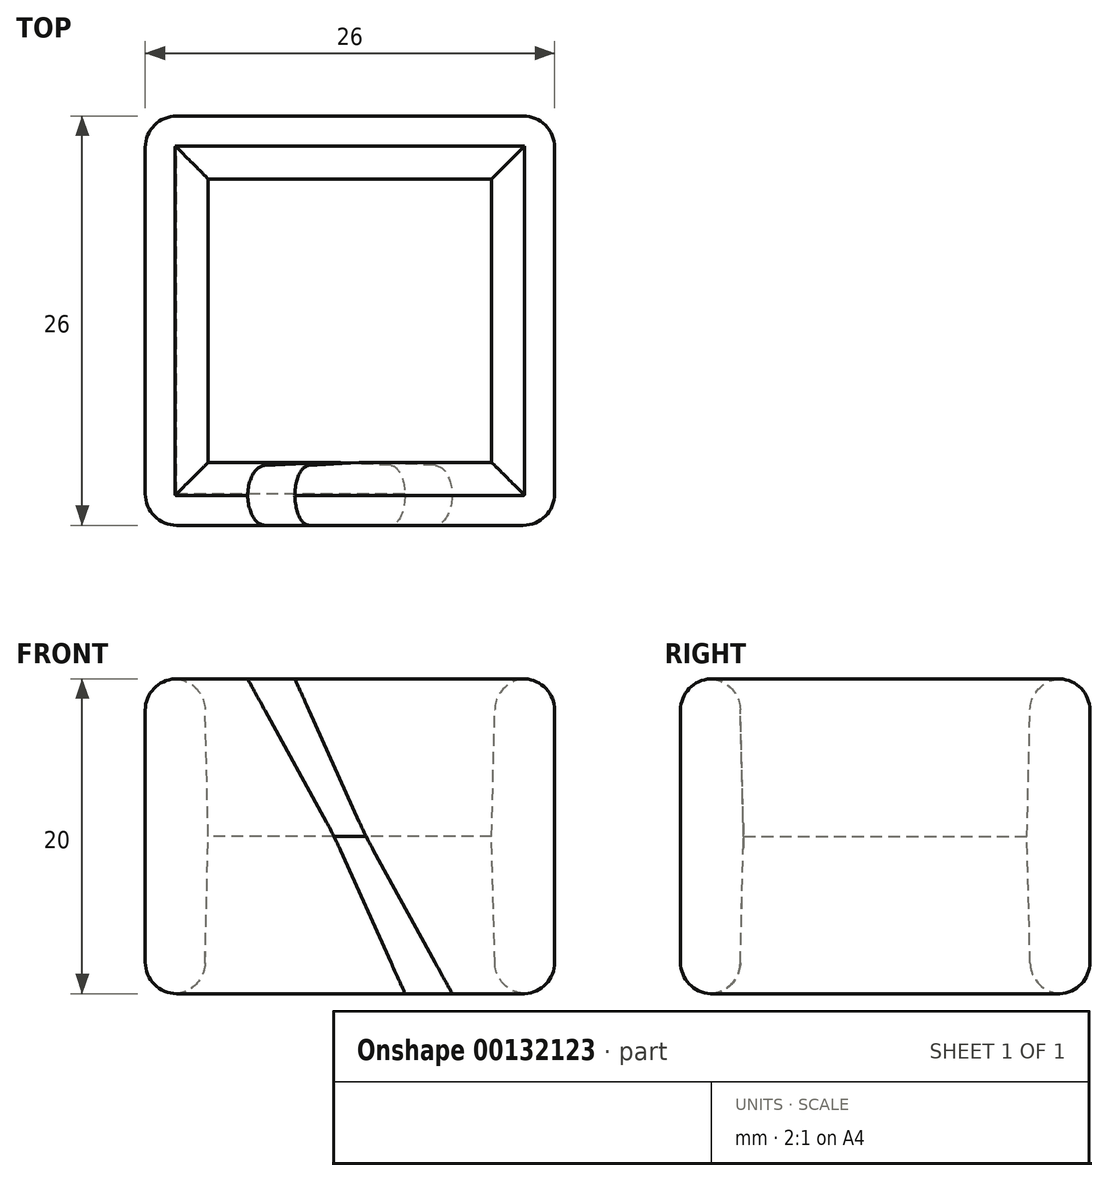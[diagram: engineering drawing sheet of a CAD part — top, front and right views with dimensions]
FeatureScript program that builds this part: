
annotation { "Feature Type Name" : "Feature", "Feature Type Description" : "" }
export const myFeature = defineFeature(function(context is Context, id is Id, definition is map)
    precondition{}
    {
        {
            var Q0;
            Q0=qCreatedBy(makeId("Top.planeOp"),FACE);
            var sketch = newSketch(context, id + "F0", { "sketchPlane" : qUnion([Q0])});
            skLineSegment(sketch, "E0.bottom", {"start": v(9.25, -9.25) * mm, "end": v(-9.25, -9.25) * mm});
            skLineSegment(sketch, "E0.top", {"start": v(9.25, 9.25) * mm, "end": v(-9.25, 9.25) * mm});
            skLineSegment(sketch, "E0.left", {"start": v(9.25, -9.25) * mm, "end": v(9.25, 9.25) * mm});
            skLineSegment(sketch, "E0.right", {"start": v(-9.25, -9.25) * mm, "end": v(-9.25, 9.25) * mm});
            skPoint(sketch, "E0.middle", {"position": v(0, 0) * mm});
            skLineSegment(sketch, "E1.bottom", {"start": v(13, -13) * mm, "end": v(-13, -13) * mm});
            skLineSegment(sketch, "E1.top", {"start": v(13, 13) * mm, "end": v(-13, 13) * mm});
            skLineSegment(sketch, "E1.left", {"start": v(13, -13) * mm, "end": v(13, 13) * mm});
            skLineSegment(sketch, "E1.right", {"start": v(-13, -13) * mm, "end": v(-13, 13) * mm});
            skLineSegment(sketch, "E2", {"start": v(-9.25, -9.25) * mm, "end": v(-13, -13) * mm});
            skLineSegment(sketch, "E3", {"start": v(9.25, 9.25) * mm, "end": v(13, 13) * mm});
            skLineSegment(sketch, "E4", {"start": v(0, -9.25) * mm, "end": v(0, -13) * mm, "construction": true});
            skLineSegment(sketch, "E5.0", {"start": v(5, -9.25) * mm, "end": v(5, -13.25) * mm, "construction": true});
            skLineSegment(sketch, "E6.0", {"start": v(6.5, -9.25) * mm, "end": v(6.5, -13.25) * mm});
            skLineSegment(sketch, "E7.0", {"start": v(3.5, -9.25) * mm, "end": v(3.5, -13.25) * mm});
            skSolve(sketch);
        }
        {
            var Q0;
            Q0=qCreatedBy(makeId("Top.planeOp"),FACE);
            cPlane(context, id + "F1", {"entities" : qUnion([Q0]), "cplaneType" : CPlaneType.OFFSET, "offset" : 10 * mm, "width" : 150 * mm, "height" : 150 * mm});
        }
        {
            var Q0;
            Q0=qCreatedBy(id+"F1.planeOp",FACE);
            var sketch = newSketch(context, id + "F2", { "sketchPlane" : qUnion([Q0])});
            skPoint(sketch, "E8.0", {"position": v(0, 0) * mm});
            skLineSegment(sketch, "E9.0", {"start": v(13, 13) * mm, "end": v(-13, 13) * mm});
            skLineSegment(sketch, "E10.0", {"start": v(-13, -13) * mm, "end": v(-13, 13) * mm});
            skLineSegment(sketch, "E11.0", {"start": v(13, -13) * mm, "end": v(-13, -13) * mm});
            skLineSegment(sketch, "E12.0", {"start": v(13, -13) * mm, "end": v(13, 13) * mm});
            skLineSegment(sketch, "E13.bottom", {"start": v(9, -9) * mm, "end": v(-9, -9) * mm});
            skLineSegment(sketch, "E13.top", {"start": v(9, 9) * mm, "end": v(-9, 9) * mm});
            skLineSegment(sketch, "E13.left", {"start": v(9, -9) * mm, "end": v(9, 9) * mm});
            skLineSegment(sketch, "E13.right", {"start": v(-9, -9) * mm, "end": v(-9, 9) * mm});
            skLineSegment(sketch, "E14", {"start": v(-13, -13) * mm, "end": v(-9, -9) * mm});
            skLineSegment(sketch, "E15", {"start": v(9, 9) * mm, "end": v(13, 13) * mm});
            skLineSegment(sketch, "E16", {"start": v(0, -9) * mm, "end": v(0, -13) * mm, "construction": true});
            skLineSegment(sketch, "E17.0", {"start": v(-1, -9) * mm, "end": v(-1, -13) * mm});
            skLineSegment(sketch, "E18.MirrorCS", {"start": v(1, -9) * mm, "end": v(1, -13) * mm});
            skSolve(sketch);
        }
        {
            var Q0;
            Q0=qCreatedBy(makeId("Top.planeOp"),FACE);
            cPlane(context, id + "F3", {"entities" : qUnion([Q0]), "cplaneType" : CPlaneType.OFFSET, "offset" : 20 * mm, "width" : 150 * mm, "height" : 150 * mm});
        }
        {
            var Q0;
            Q0=qCreatedBy(id+"F3.planeOp",FACE);
            var sketch = newSketch(context, id + "F4", { "sketchPlane" : qUnion([Q0])});
            skPoint(sketch, "E19.0", {"position": v(0, 0) * mm});
            skLineSegment(sketch, "E20.0", {"start": v(13, 13) * mm, "end": v(-13, 13) * mm});
            skLineSegment(sketch, "E21.0", {"start": v(13, -13) * mm, "end": v(13, 13) * mm});
            skLineSegment(sketch, "E21.1", {"start": v(13, -13) * mm, "end": v(-13, -13) * mm});
            skLineSegment(sketch, "E21.2", {"start": v(-13, -13) * mm, "end": v(-13, 13) * mm});
            skLineSegment(sketch, "E22.bottom", {"start": v(9.25, -9.25) * mm, "end": v(-9.25, -9.25) * mm});
            skLineSegment(sketch, "E22.top", {"start": v(9.25, 9.25) * mm, "end": v(-9.25, 9.25) * mm});
            skLineSegment(sketch, "E22.left", {"start": v(9.25, -9.25) * mm, "end": v(9.25, 9.25) * mm});
            skLineSegment(sketch, "E22.right", {"start": v(-9.25, -9.25) * mm, "end": v(-9.25, 9.25) * mm});
            skLineSegment(sketch, "E23", {"start": v(-13, -13) * mm, "end": v(-9.25, -9.25) * mm});
            skLineSegment(sketch, "E24", {"start": v(9.25, 9.25) * mm, "end": v(13, 13) * mm});
            skLineSegment(sketch, "E25", {"start": v(0, -9.25) * mm, "end": v(0, -13) * mm, "construction": true});
            skLineSegment(sketch, "E26.0", {"start": v(-5, -9.25) * mm, "end": v(-5, -13) * mm, "construction": true});
            skLineSegment(sketch, "E27.0", {"start": v(-6.5, -9.25) * mm, "end": v(-6.5, -13) * mm});
            skLineSegment(sketch, "E28.0", {"start": v(-3.5, -9.25) * mm, "end": v(-3.5, -13) * mm});
            skSolve(sketch);
        }
        {
            var Q0;
            Q0=makeQuery(id+"F0.imprint","IMPRINT",FACE,{"disambiguationData":[TD([[makeQuery(id+"F0.imprint","IMPRINT",EDGE,{"derivedFrom":sQuery(id+"F0.wireOp",EDGE,"E0.top")}),-1.0]])]});
            var Q1;
            Q1=makeQuery(id+"F2.imprint","IMPRINT",FACE,{"disambiguationData":[TD([[makeQuery(id+"F2.imprint","IMPRINT",EDGE,{"derivedFrom":sQuery(id+"F2.wireOp",EDGE,"E9.0")}),1.0]])]});
            loft(context, id + "F5", {"sheetProfilesArray" : [{ "sheetProfileEntities" : qUnion([Q0]) }, { "sheetProfileEntities" : qUnion([Q1]) }]});
        }
        {
            var Q1;
            Q1=makeQuery(id+"F2.imprint","IMPRINT",FACE,{"disambiguationData":[TD([[makeQuery(id+"F2.imprint","IMPRINT",EDGE,{"derivedFrom":sQuery(id+"F2.wireOp",EDGE,"E9.0")}),1.0]])]});
            var Q2;
            Q2=makeQuery(id+"F4.imprint","IMPRINT",FACE,{"disambiguationData":[TD([[makeQuery(id+"F4.imprint","IMPRINT",EDGE,{"derivedFrom":sQuery(id+"F4.wireOp",EDGE,"E20.0")}),1.0]])]});
            loft(context, id + "F6", {"operationType" : NewBodyOperationType.ADD, "sheetProfilesArray" : [{ "sheetProfileEntities" : qUnion([Q1]) }, { "sheetProfileEntities" : qUnion([Q2]) }]});
        }
        {
            var Q1;
            {var subQ0=sQuery(id+"F0.wireOp",EDGE,"E2");Q1=makeQuery(id+"F0.imprint","IMPRINT",FACE,{"disambiguationData":[TD([[makeQuery(id+"F0.imprint","IMPRINT",EDGE,{"derivedFrom":subQ0}),1.0]])]});}
            var Q2;
            {var subQ0=sQuery(id+"F2.wireOp",EDGE,"E14");Q2=makeQuery(id+"F2.imprint","IMPRINT",FACE,{"disambiguationData":[TD([[makeQuery(id+"F2.imprint","IMPRINT",EDGE,{"derivedFrom":subQ0}),-1.0]])]});}
            loft(context, id + "F7", {"operationType" : NewBodyOperationType.ADD, "sheetProfilesArray" : [{ "sheetProfileEntities" : qUnion([Q1]) }, { "sheetProfileEntities" : qUnion([Q2]) }]});
        }
        {
            var Q1;
            {var subQ0=sQuery(id+"F2.wireOp",EDGE,"E14");Q1=makeQuery(id+"F2.imprint","IMPRINT",FACE,{"disambiguationData":[TD([[makeQuery(id+"F2.imprint","IMPRINT",EDGE,{"derivedFrom":subQ0}),-1.0]])]});}
            var Q2;
            {var subQ0=sQuery(id+"F4.wireOp",EDGE,"E23");Q2=makeQuery(id+"F4.imprint","IMPRINT",FACE,{"disambiguationData":[TD([[makeQuery(id+"F4.imprint","IMPRINT",EDGE,{"derivedFrom":subQ0}),-1.0]])]});}
            loft(context, id + "F8", {"operationType" : NewBodyOperationType.ADD, "sheetProfilesArray" : [{ "sheetProfileEntities" : qUnion([Q1]) }, { "sheetProfileEntities" : qUnion([Q2]) }]});
        }
        {
            var Q1;
            {var subQ3=sQuery(id+"F0.wireOp",EDGE,"E0.left");Q1=makeQuery(id+"F0.imprint","IMPRINT",FACE,{"disambiguationData":[TD([[makeQuery(id+"F0.imprint","IMPRINT",EDGE,{"derivedFrom":subQ3}),-1.0]])]});}
            var Q2;
            {var subQ3=sQuery(id+"F2.wireOp",EDGE,"E12.0");Q2=makeQuery(id+"F2.imprint","IMPRINT",FACE,{"disambiguationData":[TD([[makeQuery(id+"F2.imprint","IMPRINT",EDGE,{"derivedFrom":subQ3}),1.0]])]});}
            loft(context, id + "F9", {"operationType" : NewBodyOperationType.ADD, "sheetProfilesArray" : [{ "sheetProfileEntities" : qUnion([Q1]) }, { "sheetProfileEntities" : qUnion([Q2]) }]});
        }
        {
            var Q1;
            {var subQ3=sQuery(id+"F2.wireOp",EDGE,"E12.0");Q1=makeQuery(id+"F2.imprint","IMPRINT",FACE,{"disambiguationData":[TD([[makeQuery(id+"F2.imprint","IMPRINT",EDGE,{"derivedFrom":subQ3}),1.0]])]});}
            var Q2;
            {var subQ4=sQuery(id+"F4.wireOp",EDGE,"E21.0");Q2=makeQuery(id+"F4.imprint","IMPRINT",FACE,{"disambiguationData":[TD([[makeQuery(id+"F4.imprint","IMPRINT",EDGE,{"derivedFrom":subQ4}),1.0]])]});}
            loft(context, id + "F10", {"operationType" : NewBodyOperationType.ADD, "sheetProfilesArray" : [{ "sheetProfileEntities" : qUnion([Q1]) }, { "sheetProfileEntities" : qUnion([Q2]) }]});
        }
        {
            var Q0;
            Q0=makeQuery(id+"F6.opLoft","MID_CAP_EDGE",EDGE,{"disambiguationData":[OSD([sQuery(id+"F4.wireOp",EDGE,"E22.top"),sQuery(id+"F4.wireOp",EDGE,"E22.left"),sQuery(id+"F4.wireOp",EDGE,"E22.right"),sQuery(id+"F4.wireOp",EDGE,"E24")])],"capPos":1.0});
            var Q1;
            Q1=makeQuery(id+"F10.opLoft","MID_CAP_EDGE",EDGE,{"disambiguationData":[OSD([sQuery(id+"F4.wireOp",EDGE,"E22.bottom"),sQuery(id+"F4.wireOp",EDGE,"E22.top"),sQuery(id+"F4.wireOp",EDGE,"E22.left"),sQuery(id+"F4.wireOp",EDGE,"E24")])],"capPos":1.0});
            var Q2;
            Q2=makeQuery(id+"F10.opLoft","MID_CAP_EDGE",EDGE,{"disambiguationData":[OSD([sQuery(id+"F4.wireOp",EDGE,"E22.bottom"),sQuery(id+"F4.wireOp",EDGE,"E22.left"),sQuery(id+"F4.wireOp",EDGE,"ebbac85e-4af3-46f9-9d82-f182fd674b780.MirrorCS")])],"capPos":1.0});
            var Q3;
            Q3=makeQuery(id+"F6.opLoft","MID_CAP_EDGE",EDGE,{"disambiguationData":[OSD([sQuery(id+"F4.wireOp",EDGE,"E22.bottom"),sQuery(id+"F4.wireOp",EDGE,"E22.top"),sQuery(id+"F4.wireOp",EDGE,"E22.right"),sQuery(id+"F4.wireOp",EDGE,"E23")])],"capPos":1.0});
            var Q4;
            Q4=makeQuery(id+"F8.opLoft","MID_CAP_EDGE",EDGE,{"disambiguationData":[OSD([sQuery(id+"F4.wireOp",EDGE,"E22.bottom"),sQuery(id+"F4.wireOp",EDGE,"E22.right"),sQuery(id+"F4.wireOp",EDGE,"E23"),sQuery(id+"F4.wireOp",EDGE,"E27.0")])],"capPos":1.0});
            var Q5;
            Q5=makeQuery(id+"F6.opLoft","MID_CAP_EDGE",EDGE,{"disambiguationData":[OSD([sQuery(id+"F4.wireOp",EDGE,"E20.0"),sQuery(id+"F4.wireOp",EDGE,"E21.1"),sQuery(id+"F4.wireOp",EDGE,"E21.2"),sQuery(id+"F4.wireOp",EDGE,"E23")])],"capPos":1.0});
            var Q6;
            Q6=makeQuery(id+"F8.opLoft","MID_CAP_EDGE",EDGE,{"disambiguationData":[OSD([sQuery(id+"F4.wireOp",EDGE,"E21.1"),sQuery(id+"F4.wireOp",EDGE,"E21.2"),sQuery(id+"F4.wireOp",EDGE,"E23"),sQuery(id+"F4.wireOp",EDGE,"E27.0")])],"capPos":1.0});
            var Q7;
            Q7=makeQuery(id+"F10.opLoft","MID_CAP_EDGE",EDGE,{"disambiguationData":[OSD([sQuery(id+"F4.wireOp",EDGE,"E21.0"),sQuery(id+"F4.wireOp",EDGE,"E21.1"),sQuery(id+"F4.wireOp",EDGE,"ebbac85e-4af3-46f9-9d82-f182fd674b780.MirrorCS")])],"capPos":1.0});
            var Q8;
            Q8=makeQuery(id+"F6.opLoft","MID_CAP_EDGE",EDGE,{"disambiguationData":[OSD([sQuery(id+"F4.wireOp",EDGE,"E20.0"),sQuery(id+"F4.wireOp",EDGE,"E21.0"),sQuery(id+"F4.wireOp",EDGE,"E21.2"),sQuery(id+"F4.wireOp",EDGE,"E24")])],"capPos":1.0});
            var Q9;
            Q9=makeQuery(id+"F10.opLoft","MID_CAP_EDGE",EDGE,{"disambiguationData":[OSD([sQuery(id+"F4.wireOp",EDGE,"E20.0"),sQuery(id+"F4.wireOp",EDGE,"E21.0"),sQuery(id+"F4.wireOp",EDGE,"E21.1"),sQuery(id+"F4.wireOp",EDGE,"E24")])],"capPos":1.0});
            var Q10;
            {var subQ0=sQuery(id+"F4.wireOp",EDGE,"E24");var subQ1=sQuery(id+"F4.wireOp",EDGE,"E21.0");var subQ2=sQuery(id+"F4.wireOp",EDGE,"E20.0");var subQ3=sQuery(id+"F2.wireOp",EDGE,"E15");var subQ4=sQuery(id+"F2.wireOp",EDGE,"E12.0");var subQ5=sQuery(id+"F2.wireOp",EDGE,"E9.0");var subQ6=sQuery(id+"F0.wireOp",EDGE,"E3");var subQ7=sQuery(id+"F0.wireOp",EDGE,"E1.left");var subQ8=sQuery(id+"F0.wireOp",EDGE,"E1.top");var subQ9=makeQuery(id+"F6.boolean.opBoolean","MERGE",EDGE,{"derivedFrom":[makeQuery(id+"F5.opLoft","SWEPT_EDGE",EDGE,{"disambiguationData":[OSD([subQ8,subQ7,subQ6,subQ5,subQ4,subQ3])]}),makeQuery(id+"F6.opLoft","SWEPT_EDGE",EDGE,{"disambiguationData":[OSD([subQ5,subQ4,subQ3,subQ2,subQ1,subQ0])]})]});Q10=makeQuery(id+"F10.boolean.opBoolean","MERGE",EDGE,{"derivedFrom":[makeQuery(id+"F9.boolean.opBoolean","MERGE",EDGE,{"derivedFrom":[subQ9,makeQuery(id+"F9.opLoft","SWEPT_EDGE",EDGE,{"disambiguationData":[OSD([subQ8,subQ7,subQ6,subQ5,subQ4,subQ3])]})]}),makeQuery(id+"F9.boolean.opBoolean","SPLIT",EDGE,{"derivedFrom":subQ9}),makeQuery(id+"F10.opLoft","SWEPT_EDGE",EDGE,{"disambiguationData":[OSD([subQ5,subQ4,subQ3,subQ2,subQ1,subQ0])]})]});}
            var Q11;
            {var subQ0=sQuery(id+"F2.wireOp",EDGE,"E12.0");var subQ1=sQuery(id+"F2.wireOp",EDGE,"E11.0");Q11=makeQuery(id+"F10.boolean.opBoolean","MERGE",EDGE,{"derivedFrom":[makeQuery(id+"F9.opLoft","SWEPT_EDGE",EDGE,{"disambiguationData":[OSD([sQuery(id+"F0.wireOp",EDGE,"E1.bottom"),sQuery(id+"F0.wireOp",EDGE,"E1.left"),subQ1,subQ0])]}),makeQuery(id+"F10.opLoft","SWEPT_EDGE",EDGE,{"disambiguationData":[OSD([subQ1,subQ0,sQuery(id+"F4.wireOp",EDGE,"E21.0"),sQuery(id+"F4.wireOp",EDGE,"E21.1")])]})]});}
            var Q12;
            {var subQ0=sQuery(id+"F4.wireOp",EDGE,"E23");var subQ1=sQuery(id+"F4.wireOp",EDGE,"E21.2");var subQ2=sQuery(id+"F4.wireOp",EDGE,"E21.1");var subQ3=sQuery(id+"F2.wireOp",EDGE,"E14");var subQ4=sQuery(id+"F2.wireOp",EDGE,"E11.0");var subQ5=sQuery(id+"F2.wireOp",EDGE,"E10.0");var subQ6=sQuery(id+"F0.wireOp",EDGE,"E2");var subQ7=sQuery(id+"F0.wireOp",EDGE,"E1.right");var subQ8=sQuery(id+"F0.wireOp",EDGE,"E1.bottom");var subQ9=makeQuery(id+"F6.boolean.opBoolean","MERGE",EDGE,{"derivedFrom":[makeQuery(id+"F5.opLoft","SWEPT_EDGE",EDGE,{"disambiguationData":[OSD([subQ8,subQ7,subQ6,subQ5,subQ4,subQ3])]}),makeQuery(id+"F6.opLoft","SWEPT_EDGE",EDGE,{"disambiguationData":[OSD([subQ5,subQ4,subQ3,subQ2,subQ1,subQ0])]})]});Q12=makeQuery(id+"F8.boolean.opBoolean","MERGE",EDGE,{"derivedFrom":[makeQuery(id+"F7.boolean.opBoolean","MERGE",EDGE,{"derivedFrom":[subQ9,makeQuery(id+"F7.opLoft","SWEPT_EDGE",EDGE,{"disambiguationData":[OSD([subQ8,subQ7,subQ6,subQ5,subQ4,subQ3])]})]}),makeQuery(id+"F7.boolean.opBoolean","SPLIT",EDGE,{"derivedFrom":subQ9}),makeQuery(id+"F8.opLoft","SWEPT_EDGE",EDGE,{"disambiguationData":[OSD([subQ5,subQ4,subQ3,subQ2,subQ1,subQ0])]})]});}
            var Q13;
            Q13=makeQuery(id+"F9.opLoft","MID_CAP_EDGE",EDGE,{"disambiguationData":[OSD([sQuery(id+"F0.wireOp",EDGE,"E1.bottom"),sQuery(id+"F0.wireOp",EDGE,"E1.top"),sQuery(id+"F0.wireOp",EDGE,"E1.left"),sQuery(id+"F0.wireOp",EDGE,"E3")])],"capPos":0.0});
            var Q14;
            Q14=makeQuery(id+"F5.opLoft","MID_CAP_EDGE",EDGE,{"disambiguationData":[OSD([sQuery(id+"F0.wireOp",EDGE,"E1.top"),sQuery(id+"F0.wireOp",EDGE,"E1.left"),sQuery(id+"F0.wireOp",EDGE,"E1.right"),sQuery(id+"F0.wireOp",EDGE,"E3")])],"capPos":0.0});
            var Q15;
            Q15=makeQuery(id+"F9.opLoft","MID_CAP_EDGE",EDGE,{"disambiguationData":[OSD([sQuery(id+"F0.wireOp",EDGE,"E1.bottom"),sQuery(id+"F0.wireOp",EDGE,"E1.left"),sQuery(id+"F0.wireOp",EDGE,"E6.0")])],"capPos":0.0});
            var Q16;
            Q16=makeQuery(id+"F7.opLoft","MID_CAP_EDGE",EDGE,{"disambiguationData":[OSD([sQuery(id+"F0.wireOp",EDGE,"E1.bottom"),sQuery(id+"F0.wireOp",EDGE,"E1.right"),sQuery(id+"F0.wireOp",EDGE,"E2"),sQuery(id+"F0.wireOp",EDGE,"4b8213a9-0e5b-4562-8142-2c595d69f7cd0.MirrorCS")])],"capPos":0.0});
            var Q17;
            {var subQ0=sQuery(id+"F2.wireOp",EDGE,"E10.0");var subQ1=sQuery(id+"F2.wireOp",EDGE,"E9.0");Q17=makeQuery(id+"F6.boolean.opBoolean","MERGE",EDGE,{"derivedFrom":[makeQuery(id+"F5.opLoft","SWEPT_EDGE",EDGE,{"disambiguationData":[OSD([sQuery(id+"F0.wireOp",EDGE,"E1.top"),sQuery(id+"F0.wireOp",EDGE,"E1.right"),subQ1,subQ0])]}),makeQuery(id+"F6.opLoft","SWEPT_EDGE",EDGE,{"disambiguationData":[OSD([subQ1,subQ0,sQuery(id+"F4.wireOp",EDGE,"E20.0"),sQuery(id+"F4.wireOp",EDGE,"E21.2")])]})]});}
            var Q18;
            Q18=makeQuery(id+"F5.opLoft","MID_CAP_EDGE",EDGE,{"disambiguationData":[OSD([sQuery(id+"F0.wireOp",EDGE,"E1.bottom"),sQuery(id+"F0.wireOp",EDGE,"E1.top"),sQuery(id+"F0.wireOp",EDGE,"E1.right"),sQuery(id+"F0.wireOp",EDGE,"E2")])],"capPos":0.0});
            fillet(context, id + "F11", {"entities" : qUnion([Q0, Q1, Q2, Q3, Q4, Q5, Q6, Q7, Q8, Q9, Q10, Q11, Q12, Q13, Q14, Q15, Q16, Q17, Q18]), "radius" : 2 * mm, "tangentPropagation" : true, "allowEdgeOverflow" : false});
        }
        {
            var Q0;
            {var subQ0=sQuery(id+"F2.wireOp",EDGE,"E17.0");var subQ1=sQuery(id+"F2.wireOp",EDGE,"E13.bottom");var subQ2=sQuery(id+"F2.wireOp",EDGE,"E11.0");Q0=makeQuery(id+"F8.boolean.opBoolean","MERGE",EDGE,{"derivedFrom":[makeQuery(id+"F7.opLoft","MID_CAP_EDGE",EDGE,{"disambiguationData":[OSD([subQ2,subQ1,subQ0])],"capPos":1.0}),makeQuery(id+"F8.opLoft","MID_CAP_EDGE",EDGE,{"disambiguationData":[OSD([subQ2,subQ1,subQ0])],"capPos":0.0})]});}
            var Q1;
            {var subQ0=sQuery(id+"F2.wireOp",EDGE,"E18.MirrorCS");var subQ1=sQuery(id+"F2.wireOp",EDGE,"E13.bottom");var subQ2=sQuery(id+"F2.wireOp",EDGE,"E11.0");Q1=makeQuery(id+"F10.boolean.opBoolean","MERGE",EDGE,{"derivedFrom":[makeQuery(id+"F9.opLoft","MID_CAP_EDGE",EDGE,{"disambiguationData":[OSD([subQ2,subQ1,subQ0])],"capPos":1.0}),makeQuery(id+"F10.opLoft","MID_CAP_EDGE",EDGE,{"disambiguationData":[OSD([subQ2,subQ1,subQ0])],"capPos":0.0})]});}
            fillet(context, id + "F12", {"entities" : qUnion([Q0, Q1]), "radius" : 25 * mm, "tangentPropagation" : true, "allowEdgeOverflow" : false});
        }
        {
            var Q0;
            Q0=makeQuery(id+"F7.opLoft","MID_CAP_EDGE",EDGE,{"disambiguationData":[OSD([sQuery(id+"F0.wireOp",EDGE,"E0.bottom"),sQuery(id+"F0.wireOp",EDGE,"E0.right"),sQuery(id+"F0.wireOp",EDGE,"E2"),sQuery(id+"F0.wireOp",EDGE,"E7.0")])],"capPos":0.0});
            var Q1;
            Q1=makeQuery(id+"F9.opLoft","MID_CAP_EDGE",EDGE,{"disambiguationData":[OSD([sQuery(id+"F0.wireOp",EDGE,"E0.bottom"),sQuery(id+"F0.wireOp",EDGE,"E0.left"),sQuery(id+"F0.wireOp",EDGE,"E6.0")])],"capPos":0.0});
            var Q2;
            Q2=makeQuery(id+"F9.opLoft","MID_CAP_EDGE",EDGE,{"disambiguationData":[OSD([sQuery(id+"F0.wireOp",EDGE,"E0.bottom"),sQuery(id+"F0.wireOp",EDGE,"E0.top"),sQuery(id+"F0.wireOp",EDGE,"E0.left"),sQuery(id+"F0.wireOp",EDGE,"E3")])],"capPos":0.0});
            var Q3;
            Q3=makeQuery(id+"F5.opLoft","MID_CAP_EDGE",EDGE,{"disambiguationData":[OSD([sQuery(id+"F0.wireOp",EDGE,"E0.top"),sQuery(id+"F0.wireOp",EDGE,"E0.left"),sQuery(id+"F0.wireOp",EDGE,"E0.right"),sQuery(id+"F0.wireOp",EDGE,"E3")])],"capPos":0.0});
            fillet(context, id + "F13", {"entities" : qUnion([Q0, Q1, Q2, Q3]), "radius" : 2 * mm, "tangentPropagation" : true, "allowEdgeOverflow" : false});
        }
        {
            var Q0;
            Q0=makeQuery(id+"F5.opLoft","MID_CAP_EDGE",EDGE,{"disambiguationData":[OSD([sQuery(id+"F0.wireOp",EDGE,"E0.bottom"),sQuery(id+"F0.wireOp",EDGE,"E0.top"),sQuery(id+"F0.wireOp",EDGE,"E0.right"),sQuery(id+"F0.wireOp",EDGE,"E2")])],"capPos":0.0});
            fillet(context, id + "F14", {"entities" : qUnion([Q0]), "radius" : 2 * mm, "tangentPropagation" : true, "allowEdgeOverflow" : false});
        }
    });
